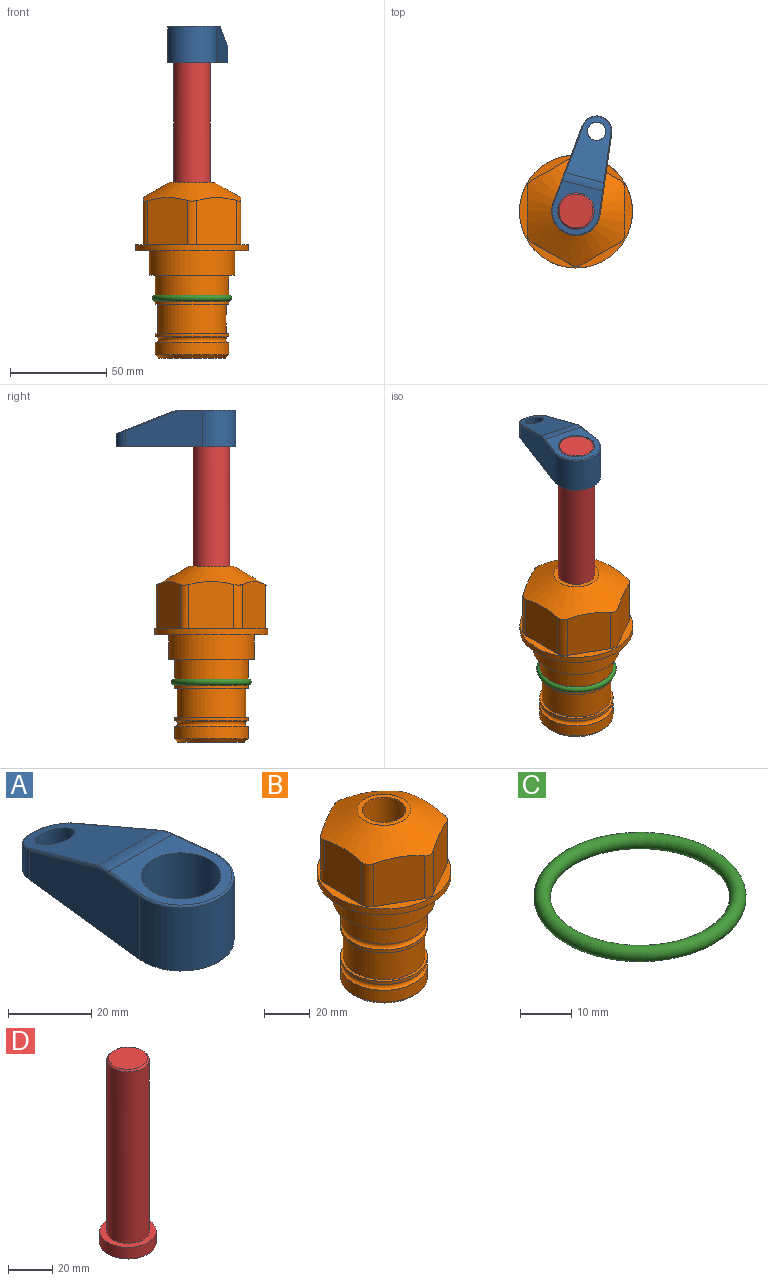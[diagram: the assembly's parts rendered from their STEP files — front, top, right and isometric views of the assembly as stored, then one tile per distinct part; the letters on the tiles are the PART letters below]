
ASSEMBLY  parts=4 mates=2
PART A: 44 faces, bbox 27.5x64.5x19.1 mm
  f0: plane 2.3x0.95mm, normal (0,0,-1), area 1mm2, adj f25,f30,f34
  f1: plane 63.5x25.4mm, normal (0,0,-1), area 561.7mm2, adj f2,f3,f4,f5,f6,f7,f19,f20
  f2: cylinder r=12.7mm len=25.4mm, axis (0,0,-1), area 792.2mm2, adj f1,f3,f5,f13
  f3: plane 42.33x18.54mm, normal (0.99,0.11,0), area 647mm2, adj f1,f2,f4,f11,f12,f14
  f4: cylinder r=7.94mm len=15.78mm, axis (0,0,-1), area 158.6mm2, adj f1,f3,f5,f16
  f5: plane 42.33x18.54mm, normal (-0.99,0.11,0), area 647mm2, adj f1,f2,f4,f15,f17,f18
  f6: cylinder r=9.53mm len=19.05mm, axis (0,0,-1), area 1140.1mm2, adj f1,f8
  f7: cylinder r=4.76mm len=10.98mm, axis (0,0,-1), area 276.1mm2, adj f1,f9
  f8: plane 25.83x24.38mm, normal (0,0,1), area 262.2mm2, adj f6,f10,f11,f13,f15
  f9: plane 32.49x20.55mm, normal (0,0.34,0.94), area 489.9mm2, adj f7,f10,f14,f16,f18
  f10: cylinder r=12.7mm len=21.49mm, axis (-1,0,0), area 93.2mm2, adj f8,f9,f12,f17
  f11: cylinder r=0.51mm len=12.34mm, axis (0.11,-0.99,0), area 9.9mm2, adj f3,f8,f12,f13
  f12: bspline ~7.62x1.64mm, area 3.5mm2, adj f3,f10,f11,f14
  f13: torus R=12.19mm, axis (0,0,1), area 33.6mm2, adj f2,f8,f11,f15
  f14: cylinder r=0.51mm len=26.01mm, axis (0.1,-0.93,0.34), area 21.6mm2, adj f3,f9,f12,f16
  f15: cylinder r=0.51mm len=12.34mm, axis (0.11,0.99,0), area 9.9mm2, adj f5,f8,f13,f17
  f16: bspline ~15.78x7.05mm, area 15.7mm2, adj f4,f9,f14,f18
  f17: bspline ~7.62x1.64mm, area 3.5mm2, adj f5,f10,f15,f18
  f18: cylinder r=0.51mm len=26.01mm, axis (0.1,0.93,-0.34), area 21.6mm2, adj f5,f9,f16,f17
  f19: plane 21.6x14.29mm, normal (-0.99,-0.11,0), area 242.6mm2, adj f1,f26,f28,f34,f36,f38
  f20: plane 21.6x14.29mm, normal (0.99,-0.11,0), area 242.6mm2, adj f1,f27,f29,f37,f39,f41
  f21: cylinder r=12.7mm len=14.29mm, axis (0,0,-1), area 173.2mm2, adj f1,f26,f27,f30,f31,f33
  f22: cylinder r=7.94mm len=7.63mm, axis (0,0,-1), area 53.8mm2, adj f1,f28,f29,f42
  f23: plane 2.3x0.95mm, normal (0,0,-1), area 1mm2, adj f25,f33,f37
  f24: plane 17.94x12.32mm, normal (0,-0.34,-0.94), area 191.2mm2, adj f25,f38,f41,f42
  f25: cylinder r=9.53mm len=12.93mm, axis (-1,0,0), area 37.5mm2, adj f0,f23,f24,f31,f36,f39
  f26: cylinder r=1.59mm len=14.29mm, axis (0,0,-1), area 49mm2, adj f1,f19,f21,f32
  f27: cylinder r=1.59mm len=14.29mm, axis (0,0,-1), area 49mm2, adj f1,f20,f21,f35
  f28: cylinder r=1.59mm len=7.28mm, axis (0,0,-1), area 22.1mm2, adj f1,f19,f22,f40
  f29: cylinder r=1.59mm len=7.28mm, axis (0,0,-1), area 22.1mm2, adj f1,f20,f22,f43
  f30: torus R=14.29mm, axis (0,0,1), area 5.8mm2, adj f0,f21,f31,f32
  f31: bspline ~11.06x2.73mm, area 20.8mm2, adj f21,f25,f30,f33
  f32: sphere r=1.59mm, area 5.4mm2, adj f26,f30,f34
  f33: torus R=14.29mm, axis (0,0,1), area 5.8mm2, adj f21,f23,f31,f35
  f34: cylinder r=1.59mm len=1.68mm, axis (-0.11,0.99,0), area 2.4mm2, adj f0,f19,f32,f36
  f35: sphere r=1.59mm, area 5.4mm2, adj f27,f33,f37
  f36: bspline ~5.82x2.33mm, area 7.7mm2, adj f19,f25,f34,f38
  f37: cylinder r=1.59mm len=1.68mm, axis (0.11,0.99,0), area 2.4mm2, adj f20,f23,f35,f39
  f38: cylinder r=1.59mm len=18.33mm, axis (0.1,-0.93,0.34), area 46.7mm2, adj f19,f24,f36,f40
  f39: bspline ~5.82x2.33mm, area 7.7mm2, adj f20,f25,f37,f41
  f40: sphere r=1.59mm, area 3.6mm2, adj f28,f38,f42
  f41: cylinder r=1.59mm len=18.33mm, axis (0.1,0.93,-0.34), area 46.7mm2, adj f20,f24,f39,f43
  f42: bspline ~8.31x1.84mm, area 15.3mm2, adj f22,f24,f40,f43
  f43: sphere r=1.59mm, area 3.6mm2, adj f29,f41,f42
PART B: 36 faces, bbox 58.7x58.7x91.2 mm
  f0: cylinder r=17.78mm len=35.56mm, axis (0,0,1), area 1670.8mm2, adj f23,f24,f31
  f1: cylinder r=19.05mm len=38.1mm, axis (0,0,1), area 1191.9mm2, adj f26,f27,f30
  f2: plane 58.66x58.66mm, normal (0,0,-1), area 1150.6mm2, adj f3,f28
  f3: cylinder r=29.33mm len=58.66mm, axis (0,0,-1), area 585.1mm2, adj f2,f4
  f4: plane 58.66x58.66mm, normal (0,0,1), area 475.9mm2, adj f3,f5,f6,f7,f8,f9,f10,f11
  f5: plane 24.5x20.32mm, normal (-0.5,0.87,0), area 562.8mm2, adj f4,f15,f16,f17
  f6: plane 24.5x20.32mm, normal (0.5,0.87,0), area 562.8mm2, adj f4,f14,f15,f17
  f7: plane 24.5x23.48mm, normal (1,0,0), area 562.8mm2, adj f4,f13,f14,f17
  f8: plane 24.5x20.32mm, normal (0.5,-0.87,0), area 562.8mm2, adj f4,f12,f13,f17
  f9: plane 24.5x20.32mm, normal (-0.5,-0.87,0), area 562.8mm2, adj f4,f11,f12,f17
  f10: plane 24.5x23.48mm, normal (-1,0,0), area 562.8mm2, adj f4,f11,f16,f17
  f11: cylinder r=5.08mm len=23.01mm, axis (0,0,-1), area 121.2mm2, adj f4,f9,f10,f17
  f12: cylinder r=5.08mm len=23.01mm, axis (0,0,-1), area 121.2mm2, adj f4,f8,f9,f17
  f13: cylinder r=5.08mm len=23.01mm, axis (0,0,-1), area 121.2mm2, adj f4,f7,f8,f17
  f14: cylinder r=5.08mm len=23.01mm, axis (0,0,-1), area 121.2mm2, adj f4,f6,f7,f17
  f15: cylinder r=5.08mm len=23.01mm, axis (0,0,-1), area 121.2mm2, adj f4,f5,f6,f17
  f16: cylinder r=5.08mm len=23.01mm, axis (0,0,-1), area 121.2mm2, adj f4,f5,f10,f17
  f17: cone r=11.73mm half-angle=60deg, axis (0,0,-1), area 2071.8mm2, adj f5,f6,f7,f8,f9,f10,f11,f12
  f18: plane 23.46x23.46mm, normal (0,0,1), area 147.4mm2, adj f17,f35
  f19: plane 34.93x34.93mm, normal (0,0,-1), area 958mm2, adj f29
  f20: cylinder r=19.05mm len=38.1mm, axis (0,0,1), area 760.1mm2, adj f21,f29
  f21: torus R=19.05mm, axis (0,0,1), area 565.3mm2, adj f20,f22
  f22: cylinder r=19.05mm len=38.1mm, axis (0,0,1), area 190mm2, adj f21,f23
  f23: plane 38.1x38.1mm, normal (0,0,1), area 146.9mm2, adj f0,f22
  f24: plane 38.1x38.1mm, normal (0,0,-1), area 146.9mm2, adj f0,f25
  f25: cylinder r=19.05mm len=38.1mm, axis (0,0,1), area 190mm2, adj f24,f26
  f26: torus R=19.05mm, axis (0,0,1), area 565.3mm2, adj f1,f25
  f27: plane 44.45x44.45mm, normal (0,0,-1), area 411.7mm2, adj f1,f28
  f28: cylinder r=22.23mm len=44.45mm, axis (0,0,1), area 1773.5mm2, adj f2,f27
  f29: cone r=19.05mm half-angle=45deg, axis (0,0,1), area 257.5mm2, adj f19,f20
  f30: cylinder r=3.17mm len=6.75mm, axis (-1,0,0), area 128mm2, adj f1,f33
  f31: cylinder r=3.17mm len=6.35mm, axis (-1,0,0), area 102.5mm2, adj f0,f33
  f32: plane 25.4x25.4mm, normal (0,0,1), area 506.7mm2, adj f33
  f33: cylinder r=12.7mm len=66.42mm, axis (0,0,-1), area 5236.2mm2, adj f30,f31,f32,f34
  f34: cone r=9.53mm half-angle=30deg, axis (0,0,-1), area 443.4mm2, adj f33,f35
  f35: cylinder r=9.53mm len=19.05mm, axis (0,0,-1), area 849mm2, adj f18,f34
PART C: 1 faces, bbox 44.7x44.7x3.2 mm
  f0: torus R=19.05mm, axis (0,0,1), area 1193.9mm2
PART D: 6 faces, bbox 25.4x25.4x101.6 mm
  f0: plane 17.46x17.46mm, normal (0,0,1), area 239.5mm2, adj f5
  f1: plane 25.4x25.4mm, normal (0,0,-1), area 506.7mm2, adj f2
  f2: cylinder r=12.7mm len=25.4mm, axis (0,0,1), area 506.7mm2, adj f1,f3
  f3: plane 25.4x25.4mm, normal (0,0,1), area 221.7mm2, adj f2,f4
  f4: cylinder r=9.53mm len=94.46mm, axis (0,0,1), area 5653mm2, adj f3,f5
  f5: cone r=8.73mm half-angle=45deg, axis (0,0,-1), area 64.4mm2, adj f0,f4
PLACE A rot(axis=(0,0,-1),14.4deg) t=(0,0,97.72)mm
PLACE B at identity fixed
PLACE C at identity
PLACE D rot(axis=(0,0,1),75.6deg) t=(0,0,43.11)mm
MATE cylindrical D.f2 <-> B.f0  axis (0,0,1) through (0,0,68.75)mm
MATE fastened A.f2 <-> D.f2  axis (0,0,-1) through (0,0,116.77)mm
